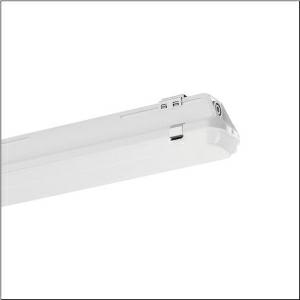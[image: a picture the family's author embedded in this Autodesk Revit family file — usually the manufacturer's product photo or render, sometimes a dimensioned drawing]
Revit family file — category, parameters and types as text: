
# Revit family: monsun_r__12_51fp20mp480h_fcdb
name_source: partatom
category: Lighting Fixtures
units: mm (PartAtom-declared; Revit-internal decimal feet)

## family parameters
Cut with Voids When Loaded = No
Host = Face
Light Source = No
Part Type = Normal
Room Calculation Point = No
Round Connector Dimension = Use Diameter
Shared = No

## types (1)
- --- (1 x LED, 8220 lm, 52.3 W, 4000K)
    Apparent Load = 52 VA
    CIE Flux Codes = 45 75 93 94 100
    Color Rendering = 80
    Color Temperature = 4000K
    Default Elevation = 1800 mm
    Description = Monsun® 12, damp-proof luminaire, chain hanger, primary optical cover: enclosure, of PC, light emission: direct distribution, primary light characteristic: symmetric, installation type: suspended mounting, surface-mounted, horizontal mounting, vertical mounting, LED rated luminous flux: 8.220 lm, light colour: 840, colour temperature: 4000K, control gear: ECG, with terminal, 3-pole, max. 2.5mm², mains connection: 220..240V, AC, 50/60Hz, rated input power: 52W, luminaire housing, of glass-fibre reinforced polyester, uncoated, bright grey, length: 1.590 mm, width: 90 mm, height: 88mm, clip for enclosure, of stainless steel (V2A), ceiling mounting element, of stainless steel (V2A), chain hanger, of stainless steel (V2A), protection rating (complete): IP66, insulation class (complete): insulation class I (protective earthing), certification: CE, ENEC, VDE, protection symbol: D, impact resistance: IK08, permissible ambient temperature for indoor applications: -35..+40°C, standard: EN 50419, EN 60598-2-1, no direct snow, no direct sun, no direct rain, for indoor or canopied outdoor use, corresponds to IFS (International Featured Standards) requirements for safety and quality in the food industry, packaging unit: 1 piece
    Height = 89 mm
    Lamp = 1 x LED
    Lamp Light Flux = 8220 lm
    Lamp Power = 52.3 W
    Lamp count = 1
    Length = 1590 mm
    Luminous efficacy = 157 lm/W
    Manufacturer = Siteco
    ModVariant = No
    Model = 51FP20MP480H
    Mounting Place = Ceiling
    Mounting Type = Pendant
    Number of Poles = 1
    OnlyDefault = Yes
    Power Factor = 1
    Product Name = Monsun® 12
    Product group = damp-proof luminaire | ceiling pendant
    ProductGroupID = 908
    Protection Class = Protection class I
    Protection Degree = IP 66
    RLX_Detail_Level = 1
    RlxData = <blob elided: 89389 chars, md5=4b50d49f>
    Socket = socket
    Standby Power = 0 W
    System Light Flux = 8220 lm
    System Power = 52 W
    Type Comments = factory setting: luminous flux: 100 % | (A | C | E) | 120 mA
    Type Image = l_1004748.jpg
    URL = http://relux.com
    VarID = @adj_134009
    Voltage = 0 V
    Weight = 0.00 kg
    Width = 90 mm

## geometry (parser evidence)
native form markers: Blend x4, Sweep x15
no freeform markers — native parametric forms only
